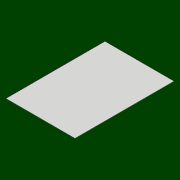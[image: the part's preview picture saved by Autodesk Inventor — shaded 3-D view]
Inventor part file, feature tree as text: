
AUTODESK INVENTOR PART (.ipt)
format: ipt  version: 2018 (Build 220112000, 112)  size: 72,192 bytes
history: native  units: mm
features: other x1, extrude x1, sketch x1
ambient origin geometry x8: Origin, YZ Plane, XZ Plane, XY Plane, X Axis, Y Axis, Z Axis, Center Point
bodies: Body1 (feature_tree)
feature tree (3):
  other  "ソリッド1"
  extrude  "押し出し1"  Depth=230.0mm
  sketch  "スケッチ1"
